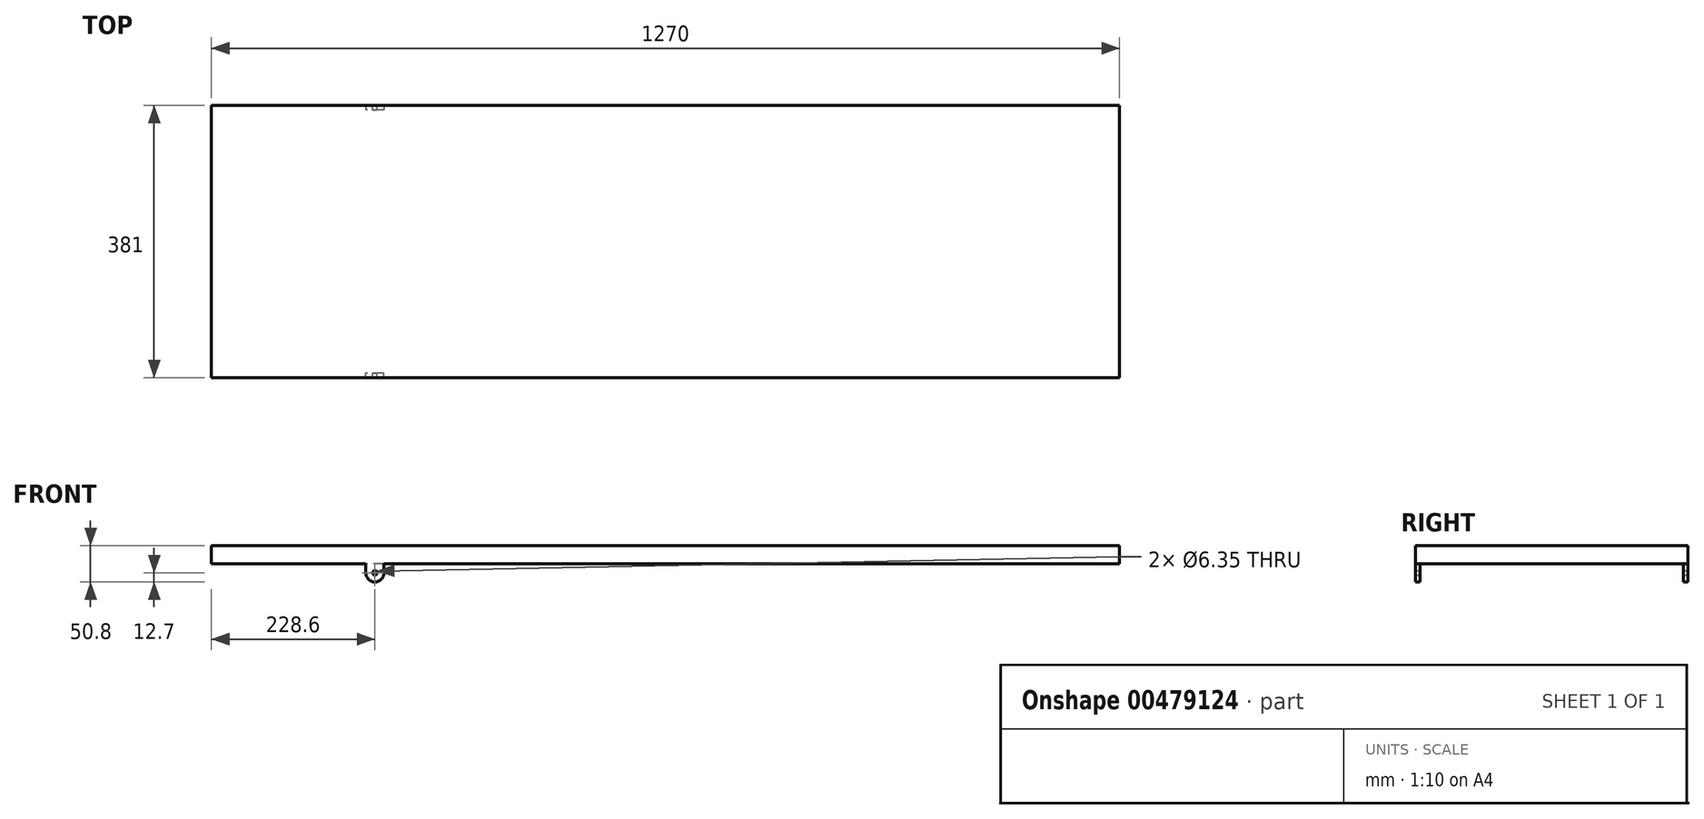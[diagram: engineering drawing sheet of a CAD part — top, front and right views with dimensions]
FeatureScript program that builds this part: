
annotation { "Feature Type Name" : "Feature", "Feature Type Description" : "" }
export const myFeature = defineFeature(function(context is Context, id is Id, definition is map)
    precondition{}
    {
        {
            var Q0;
            Q0=qCreatedBy(makeId("Top.planeOp"),FACE);
            var sketch = newSketch(context, id + "F0", { "sketchPlane" : qUnion([Q0])});
            skLineSegment(sketch, "E0.bottom", {"start": v(-635, -190.5) * mm, "end": v(635, -190.5) * mm});
            skLineSegment(sketch, "E0.top", {"start": v(-635, 190.5) * mm, "end": v(635, 190.5) * mm});
            skLineSegment(sketch, "E0.left", {"start": v(-635, -190.5) * mm, "end": v(-635, 190.5) * mm});
            skLineSegment(sketch, "E0.right", {"start": v(635, -190.5) * mm, "end": v(635, 190.5) * mm});
            skPoint(sketch, "E0.middle", {"position": v(0, 0) * mm});
            skSolve(sketch);
        }
        {
            var Q0;
            Q0 = qSketchRegion(id + "F0", true);
            extrude(context, id + "F1", {"entities" : qUnion([Q0]), "depth" : 25.4 * mm});
        }
        {
            var Q0;
            Q0=makeQuery(id+"F1.opExtrude","CAP_FACE",FACE,{"disambiguationData":[OSD([sQuery(id+"F0.wireOp",EDGE,"E0.bottom"),sQuery(id+"F0.wireOp",EDGE,"E0.top"),sQuery(id+"F0.wireOp",EDGE,"E0.left"),sQuery(id+"F0.wireOp",EDGE,"E0.right")])],"isStart":true});
            var sketch = newSketch(context, id + "F2", { "sketchPlane" : qUnion([Q0])});
            skLineSegment(sketch, "E1", {"start": v(-406.4, 190.5) * mm, "end": v(-406.4, -190.5) * mm, "construction": true});
            skLineSegment(sketch, "E2.bottom", {"start": v(-393.7, 190.5) * mm, "end": v(-419.1, 190.5) * mm});
            skLineSegment(sketch, "E2.top", {"start": v(-393.7, 184.15) * mm, "end": v(-419.1, 184.15) * mm});
            skLineSegment(sketch, "E2.left", {"start": v(-393.7, 190.5) * mm, "end": v(-393.7, 184.15) * mm});
            skLineSegment(sketch, "E2.right", {"start": v(-419.1, 190.5) * mm, "end": v(-419.1, 184.15) * mm});
            skPoint(sketch, "E2.middle", {"position": v(-406.4, 187.32) * mm});
            skLineSegment(sketch, "E3.bottom", {"start": v(-393.7, -190.5) * mm, "end": v(-419.1, -190.5) * mm});
            skLineSegment(sketch, "E3.top", {"start": v(-393.7, -184.15) * mm, "end": v(-419.1, -184.15) * mm});
            skLineSegment(sketch, "E3.left", {"start": v(-393.7, -190.5) * mm, "end": v(-393.7, -184.15) * mm});
            skLineSegment(sketch, "E3.right", {"start": v(-419.1, -190.5) * mm, "end": v(-419.1, -184.15) * mm});
            skPoint(sketch, "E3.middle", {"position": v(-406.4, -187.32) * mm});
            skLineSegment(sketch, "E4", {"start": v(-406.4, 0) * mm, "end": v(-635, 0) * mm, "construction": true});
            skSolve(sketch);
        }
        {
            var Q0;
            Q0 = qSketchRegion(id + "F2", true);
            extrude(context, id + "F3", {"entities" : qUnion([Q0]), "operationType" : NewBodyOperationType.ADD, "depth" : 25.4 * mm});
        }
        {
            var Q0;
            Q0=makeQuery(id+"F3.opExtrude","CAP_EDGE",EDGE,{"disambiguationData":[OSD([sQuery(id+"F2.wireOp",EDGE,"E2.right")])],"isStart":false});
            var Q1;
            Q1=makeQuery(id+"F3.opExtrude","CAP_EDGE",EDGE,{"disambiguationData":[OSD([sQuery(id+"F2.wireOp",EDGE,"E2.left")])],"isStart":false});
            var Q2;
            Q2=makeQuery(id+"F3.opExtrude","CAP_EDGE",EDGE,{"disambiguationData":[OSD([sQuery(id+"F2.wireOp",EDGE,"E3.right")])],"isStart":false});
            var Q3;
            Q3=makeQuery(id+"F3.opExtrude","CAP_EDGE",EDGE,{"disambiguationData":[OSD([sQuery(id+"F2.wireOp",EDGE,"E3.left")])],"isStart":false});
            fillet(context, id + "F4", {"entities" : qUnion([Q0, Q1, Q2, Q3]), "radius" : 12.7 * mm, "tangentPropagation" : true, "allowEdgeOverflow" : false});
        }
        {
            var Q0;
            Q0=makeQuery(id+"F3.boolean.opBoolean","MERGE",FACE,{"derivedFrom":[makeQuery(id+"F1.opExtrude","SWEPT_FACE",FACE,{"disambiguationData":[OSD([sQuery(id+"F0.wireOp",EDGE,"E0.top")])]}),makeQuery(id+"F3.opExtrude","SWEPT_FACE",FACE,{"disambiguationData":[OSD([sQuery(id+"F2.wireOp",EDGE,"E3.bottom")])]})]});
            var sketch = newSketch(context, id + "F5", { "sketchPlane" : qUnion([Q0])});
            skCircle(sketch, "E5", {"center": v(406.4, -12.7) * mm, "radius": 3.18 * mm});
            skSolve(sketch);
        }
        {
            var Q0;
            Q0 = qSketchRegion(id + "F5", true);
            extrude(context, id + "F6", {"entities" : qUnion([Q0]), "operationType" : NewBodyOperationType.REMOVE, "endBound" : BoundingType.THROUGH_ALL, "oppositeDirection" : true, "depth" : 25.4 * mm});
        }
    });
